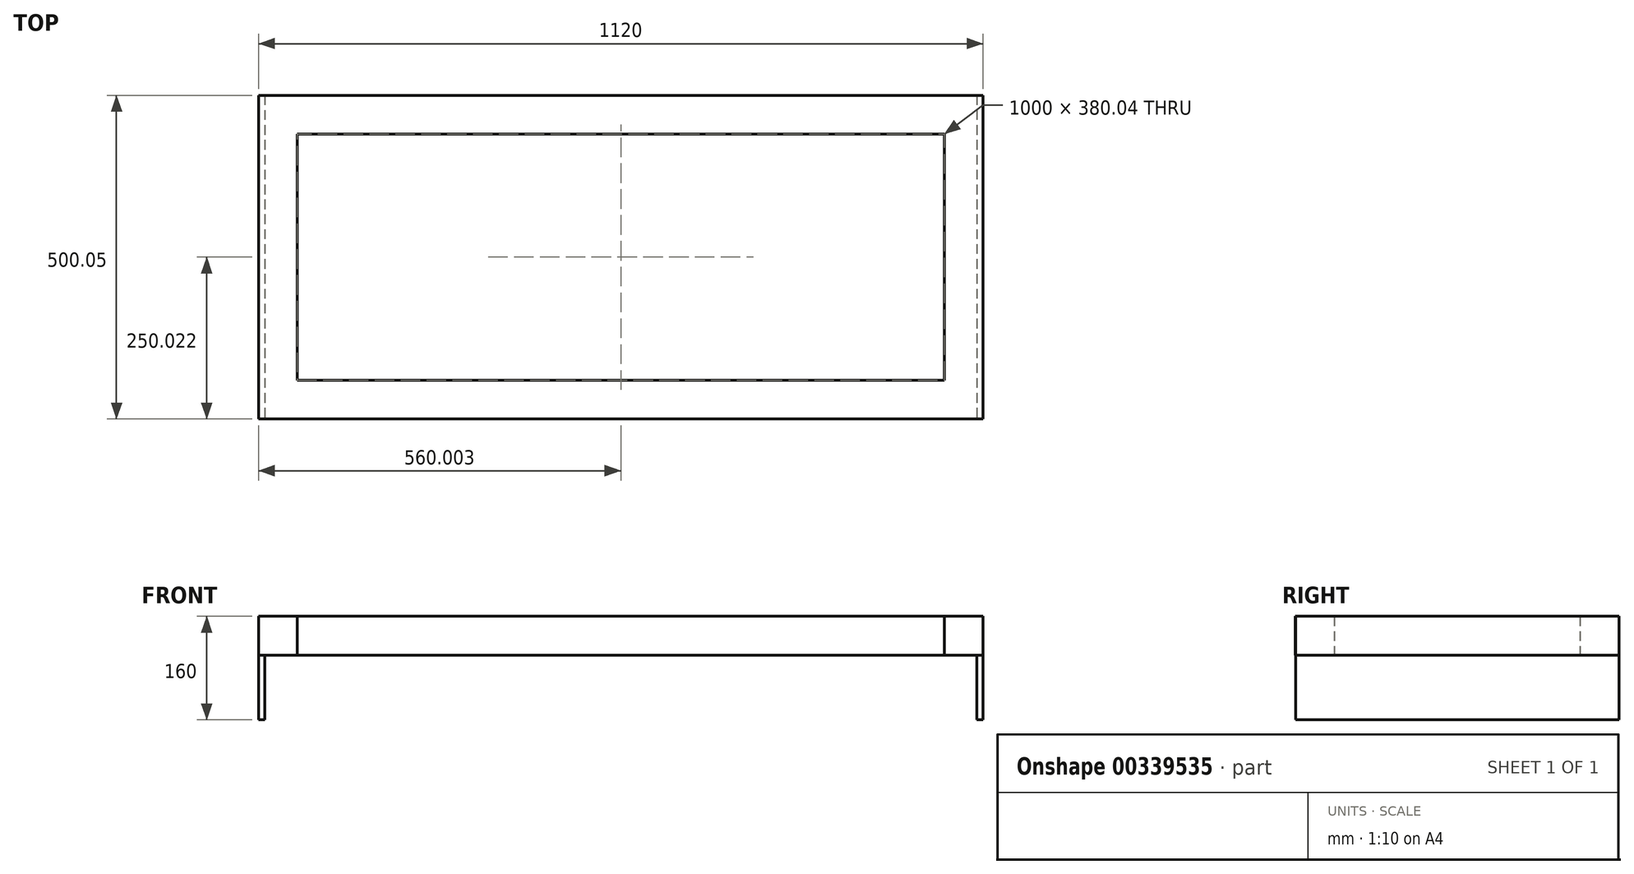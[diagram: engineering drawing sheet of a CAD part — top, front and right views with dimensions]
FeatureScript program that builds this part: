
annotation { "Feature Type Name" : "Feature", "Feature Type Description" : "" }
export const myFeature = defineFeature(function(context is Context, id is Id, definition is map)
    precondition{}
    {
        {
            var Q0;
            Q0=qCreatedBy(makeId("Top.planeOp"),FACE);
            var sketch = newSketch(context, id + "F0", { "sketchPlane" : qUnion([Q0])});
            skLineSegment(sketch, "E0.bottom", {"start": v(870.84, 622.13) * mm, "end": v(1870.84, 622.13) * mm});
            skLineSegment(sketch, "E0.top", {"start": v(870.84, 562.13) * mm, "end": v(1870.84, 562.13) * mm});
            skLineSegment(sketch, "E0.left", {"start": v(870.84, 622.13) * mm, "end": v(870.84, 562.13) * mm});
            skLineSegment(sketch, "E0.right", {"start": v(1870.84, 622.13) * mm, "end": v(1870.84, 562.13) * mm});
            skLineSegment(sketch, "E1.bottom", {"start": v(870.84, 1062.17) * mm, "end": v(1870.84, 1062.17) * mm});
            skLineSegment(sketch, "E1.top", {"start": v(870.84, 1002.17) * mm, "end": v(1870.84, 1002.17) * mm});
            skLineSegment(sketch, "E1.left", {"start": v(870.84, 1062.17) * mm, "end": v(870.84, 1002.17) * mm});
            skLineSegment(sketch, "E1.right", {"start": v(1870.84, 1062.17) * mm, "end": v(1870.84, 1002.17) * mm});
            skLineSegment(sketch, "E2.bottom", {"start": v(1870.84, 562.17) * mm, "end": v(1930.84, 562.17) * mm});
            skLineSegment(sketch, "E2.top", {"start": v(1870.84, 1062.17) * mm, "end": v(1930.84, 1062.17) * mm});
            skLineSegment(sketch, "E2.left", {"start": v(1870.84, 562.17) * mm, "end": v(1870.84, 1062.17) * mm});
            skLineSegment(sketch, "E2.right", {"start": v(1930.84, 562.17) * mm, "end": v(1930.84, 1062.17) * mm});
            skLineSegment(sketch, "E3.bottom", {"start": v(810.84, 562.18) * mm, "end": v(870.84, 562.18) * mm});
            skLineSegment(sketch, "E3.top", {"start": v(810.84, 1062.18) * mm, "end": v(870.84, 1062.18) * mm});
            skLineSegment(sketch, "E3.left", {"start": v(810.84, 562.18) * mm, "end": v(810.84, 1062.18) * mm});
            skLineSegment(sketch, "E3.right", {"start": v(870.84, 562.18) * mm, "end": v(870.84, 1062.18) * mm});
            skLineSegment(sketch, "E4", {"start": v(820.84, 1062.18) * mm, "end": v(820.84, 562.18) * mm});
            skLineSegment(sketch, "E5", {"start": v(1920.84, 1062.17) * mm, "end": v(1920.84, 562.17) * mm});
            skSolve(sketch);
        }
        {
            var Q0;
            Q0 = qSketchRegion(id + "F0", true);
            extrude(context, id + "F1", {"entities" : qUnion([Q0]), "depth" : 60 * mm, "offsetDistance" : 25 * mm});
        }
        {
            var Q0;
            {var subQ0=sQuery(id+"F0.wireOp",EDGE,"E2.right");Q0=makeQuery(id+"F0.imprint","IMPRINT",FACE,{"disambiguationData":[TD([[makeQuery(id+"F0.imprint","IMPRINT",EDGE,{"derivedFrom":subQ0}),1.0]])]});}
            var Q1;
            {var subQ2=sQuery(id+"F0.wireOp",EDGE,"E3.left");Q1=makeQuery(id+"F0.imprint","IMPRINT",FACE,{"disambiguationData":[TD([[makeQuery(id+"F0.imprint","IMPRINT",EDGE,{"derivedFrom":subQ2}),-1.0]])]});}
            extrude(context, id + "F2", {"entities" : qUnion([Q0, Q1]), "oppositeDirection" : true, "depth" : 100 * mm, "offsetDistance" : 25 * mm});
        }
    });
